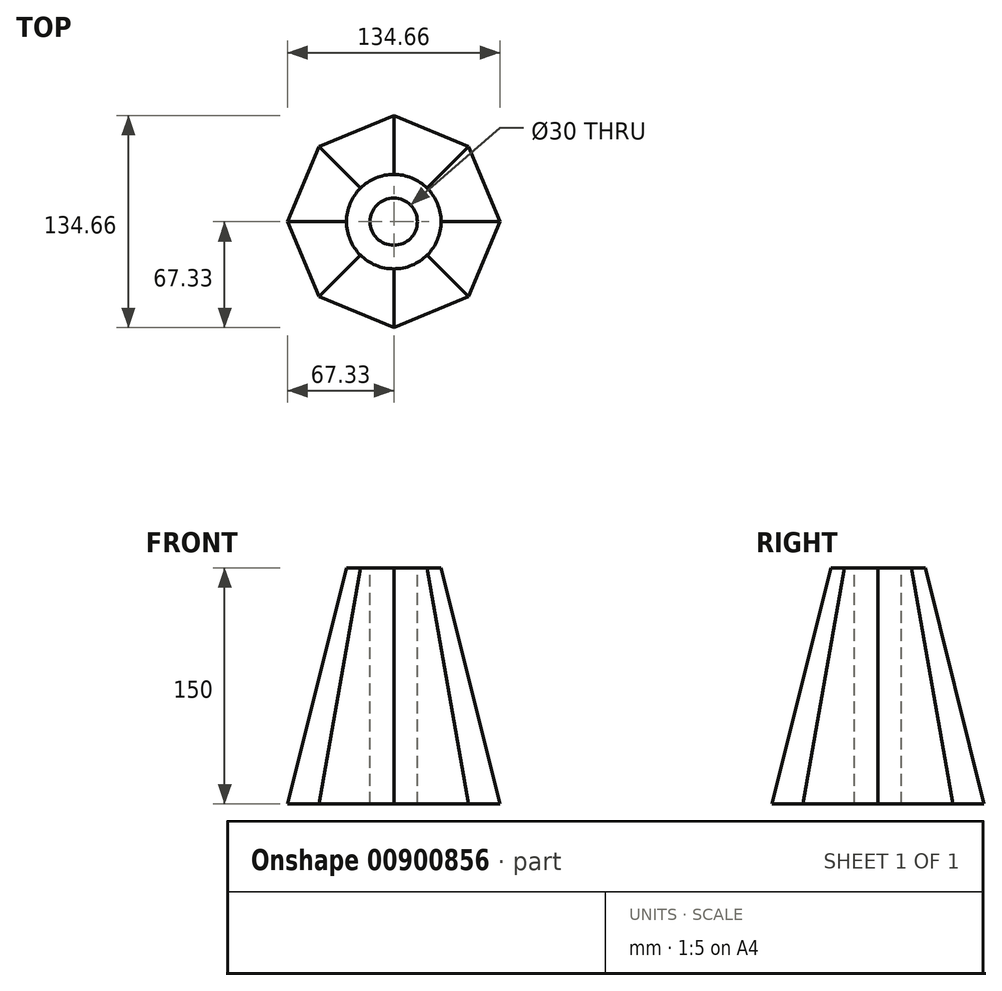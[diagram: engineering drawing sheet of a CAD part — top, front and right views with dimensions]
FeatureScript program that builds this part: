
annotation { "Feature Type Name" : "Feature", "Feature Type Description" : "" }
export const myFeature = defineFeature(function(context is Context, id is Id, definition is map)
    precondition{}
    {
        {
            var Q0;
            Q0=qCreatedBy(makeId("Top.planeOp"),FACE);
            var sketch = newSketch(context, id + "F0", { "sketchPlane" : qUnion([Q0])});
            skCircle(sketch, "E0.cCircle", {"center": v(0, 0) * mm, "radius": 62.2 * mm, "construction": true});
            skLineSegment(sketch, "E0.0", {"start": v(-67.33, 0) * mm, "end": v(-47.61, 47.61) * mm});
            skLineSegment(sketch, "E0.1", {"start": v(-47.61, 47.61) * mm, "end": v(0, 67.33) * mm});
            skLineSegment(sketch, "E0.2", {"start": v(0, 67.33) * mm, "end": v(47.61, 47.61) * mm});
            skLineSegment(sketch, "E0.3", {"start": v(47.61, 47.61) * mm, "end": v(67.33, 0) * mm});
            skLineSegment(sketch, "E0.4", {"start": v(67.33, 0) * mm, "end": v(47.61, -47.61) * mm});
            skLineSegment(sketch, "E0.5", {"start": v(47.61, -47.61) * mm, "end": v(0, -67.33) * mm});
            skLineSegment(sketch, "E0.6", {"start": v(0, -67.33) * mm, "end": v(-47.61, -47.61) * mm});
            skLineSegment(sketch, "E0.7", {"start": v(-47.61, -47.61) * mm, "end": v(-67.33, 0) * mm});
            skPoint(sketch, "E0.0.midPoint", {"position": v(-57.47, 23.8) * mm});
            skSolve(sketch);
        }
        {
            var Q0;
            Q0=qCreatedBy(makeId("Top.planeOp"),FACE);
            cPlane(context, id + "F1", {"entities" : qUnion([Q0]), "cplaneType" : CPlaneType.OFFSET, "offset" : 150 * mm, "width" : 150 * mm, "height" : 150 * mm});
        }
        {
            var Q0;
            Q0=qCreatedBy(id+"F1.planeOp",FACE);
            var sketch = newSketch(context, id + "F2", { "sketchPlane" : qUnion([Q0])});
            skCircle(sketch, "E1", {"center": v(0, 0) * mm, "radius": 30 * mm});
            skSolve(sketch);
        }
        {
            var Q0;
            Q0=makeQuery(id+"F0.imprint","IMPRINT",FACE,{"disambiguationData":[TD([[makeQuery(id+"F0.imprint","IMPRINT",EDGE,{"derivedFrom":sQuery(id+"F0.wireOp",EDGE,"E0.0")}),-1.0]])]});
            var Q1;
            Q1=makeQuery(id+"F2.imprint","IMPRINT",FACE,{"disambiguationData":[TD([[makeQuery(id+"F2.imprint","IMPRINT",EDGE,{"derivedFrom":sQuery(id+"F2.wireOp",EDGE,"E1")}),1.0]])]});
            loft(context, id + "F3", {"sheetProfilesArray" : [{ "sheetProfileEntities" : qUnion([Q0]) }, { "sheetProfileEntities" : qUnion([Q1]) }]});
        }
        {
            var Q0;
            Q0=qCreatedBy(id+"F1.planeOp",FACE);
            var sketch = newSketch(context, id + "F4", { "sketchPlane" : qUnion([Q0])});
            skCircle(sketch, "E2", {"center": v(0, 0) * mm, "radius": 15 * mm});
            skSolve(sketch);
        }
        {
            var Q0;
            Q0 = qSketchRegion(id + "F4", true);
            extrude(context, id + "F5", {"entities" : qUnion([Q0]), "operationType" : NewBodyOperationType.REMOVE, "oppositeDirection" : true, "depth" : 226.1 * mm, "offsetDistance" : 25 * mm});
        }
    });
